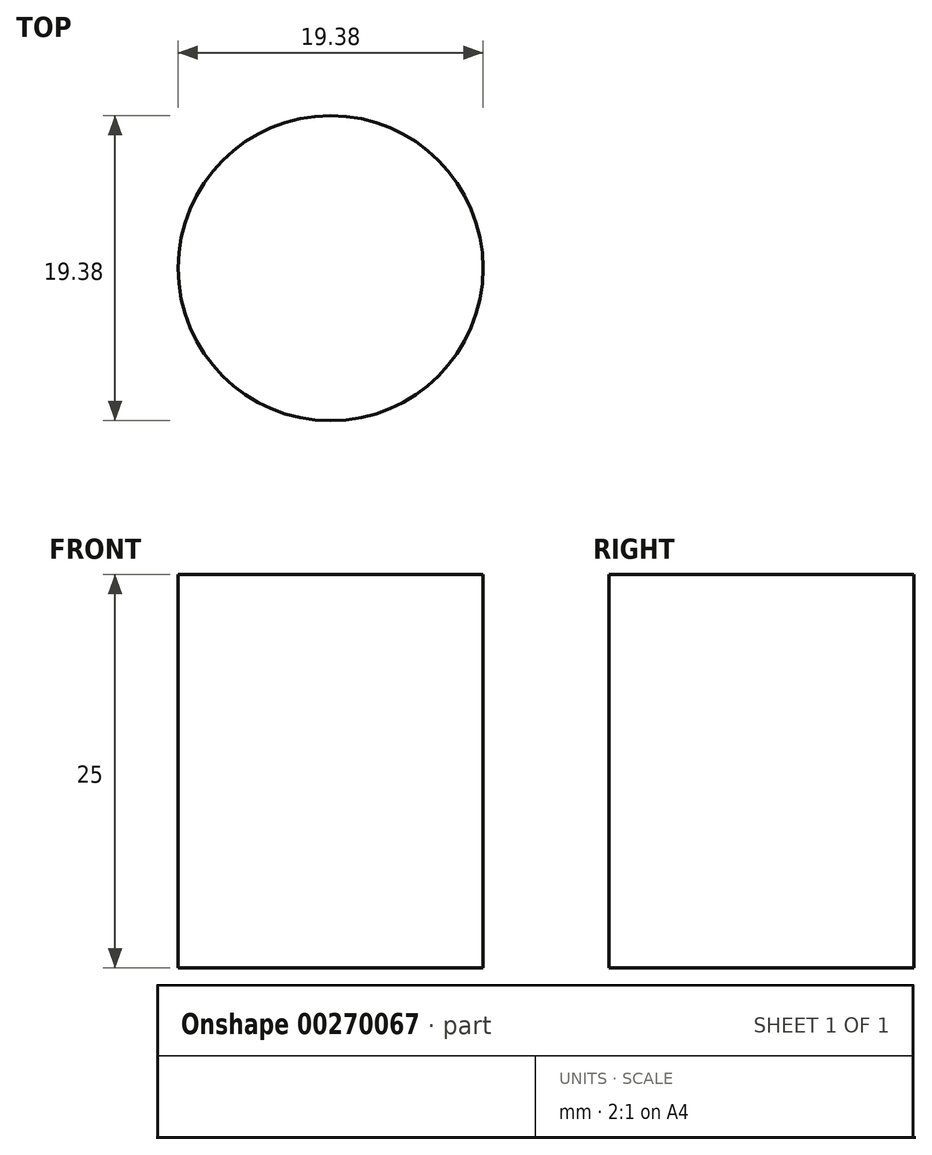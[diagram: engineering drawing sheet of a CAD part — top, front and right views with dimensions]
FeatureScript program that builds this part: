
annotation { "Feature Type Name" : "Feature", "Feature Type Description" : "" }
export const myFeature = defineFeature(function(context is Context, id is Id, definition is map)
    precondition{}
    {
        {
            var Q0;
            Q0=qCreatedBy(makeId("Top.planeOp"),FACE);
            var sketch = newSketch(context, id + "F0", { "sketchPlane" : qUnion([Q0])});
            skCircle(sketch, "E0", {"center": v(0, 0) * mm, "radius": 9.69 * mm});
            skCircle(sketch, "E1", {"center": v(0, 0) * mm, "radius": 15.22 * mm});
            skSolve(sketch);
        }
        {
            var Q0;
            Q0=makeQuery(id+"F0.imprint","IMPRINT",FACE,{"disambiguationData":[TD([[makeQuery(id+"F0.imprint","IMPRINT",EDGE,{"derivedFrom":sQuery(id+"F0.wireOp",EDGE,"E0")}),1.0]])]});
            extrude(context, id + "F1", {"entities" : qUnion([Q0]), "depth" : 25 * mm});
        }
    });
